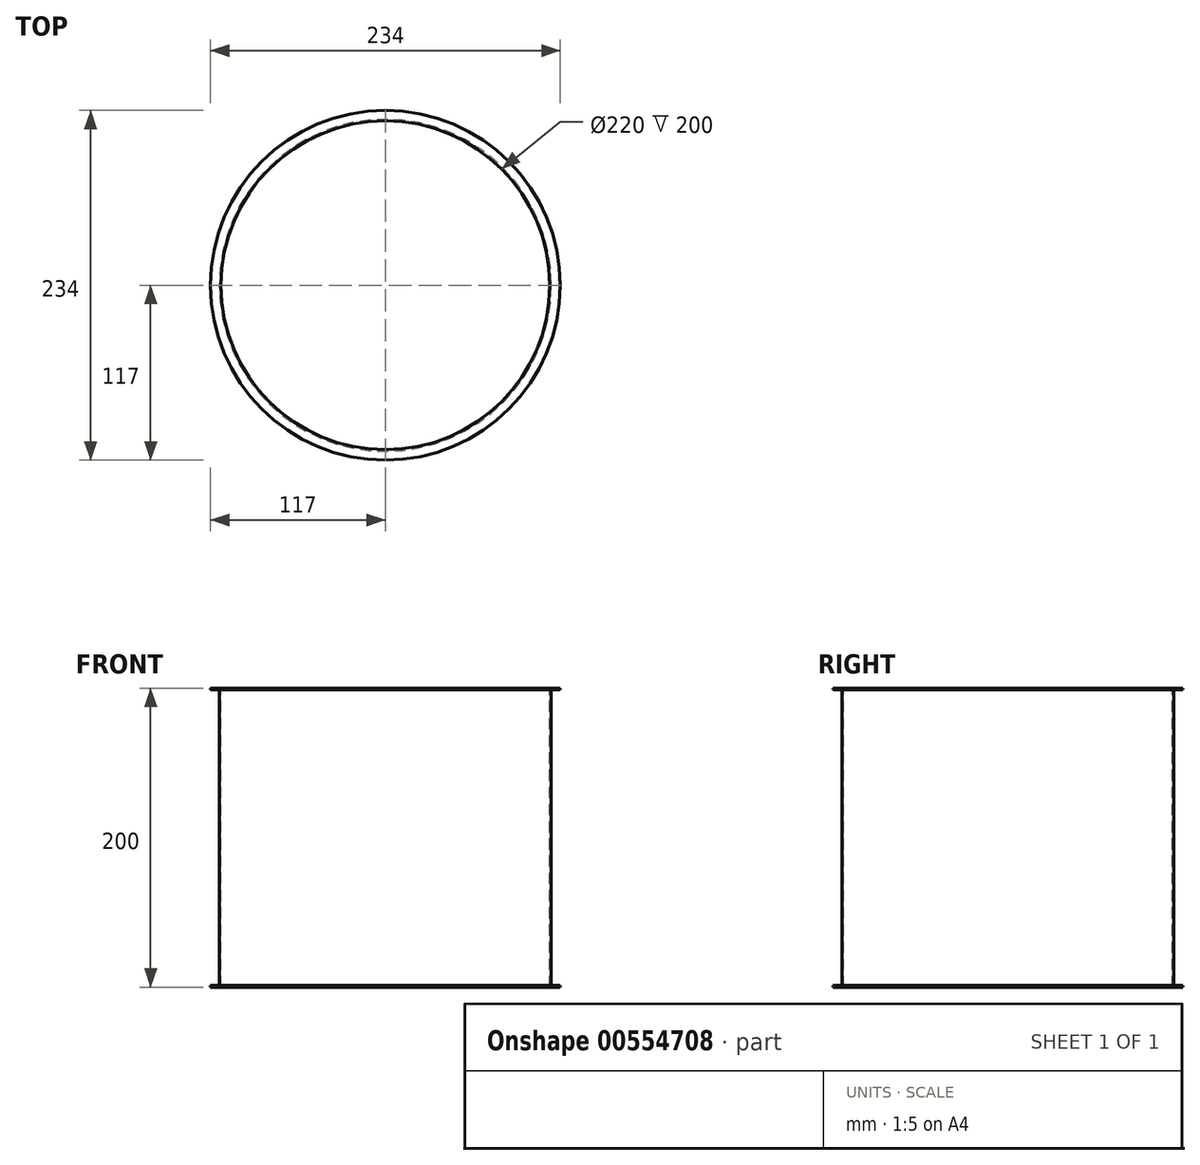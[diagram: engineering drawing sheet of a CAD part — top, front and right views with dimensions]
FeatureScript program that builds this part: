
annotation { "Feature Type Name" : "Feature", "Feature Type Description" : "" }
export const myFeature = defineFeature(function(context is Context, id is Id, definition is map)
    precondition{}
    {
        {
            var Q0;
            Q0=qCreatedBy(makeId("Front.planeOp"),FACE);
            var sketch = newSketch(context, id + "F0", { "sketchPlane" : qUnion([Q0])});
            skLineSegment(sketch, "E0.bottom", {"start": v(0, 100) * mm, "end": v(-110, 100) * mm});
            skLineSegment(sketch, "E0.top", {"start": v(0, 0) * mm, "end": v(-110, 0) * mm});
            skLineSegment(sketch, "E0.left", {"start": v(0, 100) * mm, "end": v(0, 0) * mm});
            skLineSegment(sketch, "E0.right", {"start": v(-110, 100) * mm, "end": v(-110, 0) * mm});
            skLineSegment(sketch, "E1", {"start": v(-110, 0) * mm, "end": v(-111, 0) * mm});
            skLineSegment(sketch, "E2", {"start": v(-111, 0) * mm, "end": v(-111, 99) * mm});
            skLineSegment(sketch, "E3", {"start": v(-111, 99) * mm, "end": v(-117, 99) * mm});
            skLineSegment(sketch, "E4", {"start": v(-117, 99) * mm, "end": v(-117, 100) * mm});
            skLineSegment(sketch, "E5", {"start": v(-117, 100) * mm, "end": v(-110, 100) * mm});
            skLineSegment(sketch, "E6.MirrorCS", {"start": v(0, -100) * mm, "end": v(-110, -100) * mm});
            skLineSegment(sketch, "E7.MirrorCS", {"start": v(-117, -99) * mm, "end": v(-117, -100) * mm});
            skLineSegment(sketch, "E8.MirrorCS", {"start": v(-111, -99) * mm, "end": v(-117, -99) * mm});
            skLineSegment(sketch, "E9.MirrorCS", {"start": v(-117, -100) * mm, "end": v(-110, -100) * mm});
            skLineSegment(sketch, "E10.MirrorCS", {"start": v(-110, -100) * mm, "end": v(-110, 0) * mm});
            skLineSegment(sketch, "E11.MirrorCS", {"start": v(-111, 0) * mm, "end": v(-111, -99) * mm});
            skSolve(sketch);
        }
        {
            var Q0;
            Q0=makeQuery(id+"F0.imprint","IMPRINT",FACE,{"disambiguationData":[TD([[makeQuery(id+"F0.imprint","IMPRINT",EDGE,{"derivedFrom":sQuery(id+"F0.wireOp",EDGE,"E0.right")}),-1.0]])]});
            var Q1;
            Q1=makeQuery(id+"F0.imprint","IMPRINT",FACE,{"disambiguationData":[TD([[makeQuery(id+"F0.imprint","IMPRINT",EDGE,{"derivedFrom":sQuery(id+"F0.wireOp",EDGE,"E1")}),1.0]])]});
            var Q2;
            Q2=sQuery(id+"F0.wireOp",EDGE,"E0.left");
            revolve(context, id + "F1", {"entities" : qUnion([Q0, Q1]), "axis" : qUnion([Q2]), "revolveType" : RevolveType.FULL});
        }
    });
